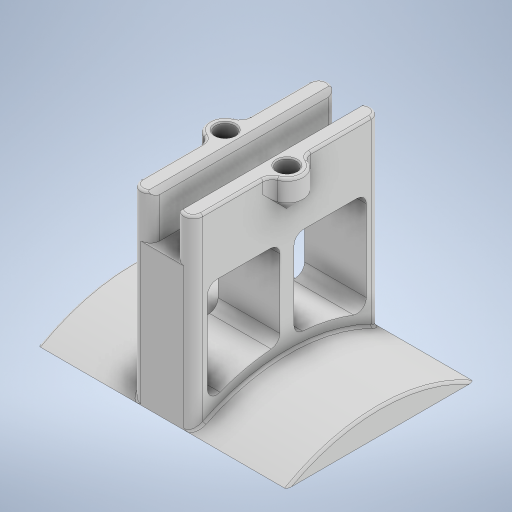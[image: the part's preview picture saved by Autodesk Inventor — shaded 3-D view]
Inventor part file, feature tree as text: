
AUTODESK INVENTOR PART (.ipt)
format: ipt  version: 2023 (Build 270158000, 158)  size: 468,992 bytes
history: native  units: mm
features: extrude x6, sketch x5, fillet x4, chamfer x3, plane x1, mirror x1
ambient origin geometry x8: Origin, YZ Plane, XZ Plane, XY Plane, X Axis, Y Axis, Z Axis, Center Point
bodies: Solid1 (feature_tree)
feature tree (20):
  extrude  "Extrusion1"  Depth=40.0mm
  extrude  "Extrusion2"  Depth=20.0mm TaperAngle=0.0deg
  plane  "Work Plane1"
  mirror  "Mirror1"
  extrude  "Extrusion3"  Depth=5.2mm
  sketch  "Sketch4"  dims[d9=4.0mm d10=9.6mm d11=0.0mm]
  extrude  "Extrusion4"  Depth=9.6mm TaperAngle=0.0deg
  extrude  "Extrusion5"  Depth=2.0mm TaperAngle=45.0deg
  extrude  "Extrusion6"  Depth=1.5mm
  chamfer  "Chamfer2"  Distance=7.0mm
  fillet  "Fillet1"  Radius=8.0mm
  chamfer  "Chamfer1"  Distance=3.1mm
  fillet  "Fillet2"  Radius=2.0mm
  fillet  "Fillet3"  Radius=2.0mm
  chamfer  "Chamfer3"  Distance=0.5mm
  fillet  "Fillet4"  Radius=2.0mm
  sketch  "Sketch1"  dims[d0=40.0mm d1=40.0mm]
  sketch  "Sketch2"  dims[d2=13.2mm d3=0.0mm d5=20.0mm d6=0.0mm]
  sketch  "Sketch3"  dims[d7=-6.6mm d8=5.2mm]
  sketch  "Sketch5"  dims[d12=2.0mm d13=1.0mm d14=2.0mm d15=45.0deg d16=4.1mm d17=7.0mm d18=8.0mm d19=0.0mm d20=3.1mm d21=0.0mm d22=3.5mm d23=2.0mm d24=45.0deg d25=2.0mm d26=0.5mm d27=0.25mm d28=2.0mm d29=45.0deg d30=40.0mm d31=3.0mm d32=3.0mm d33=4.0mm d34=4.0mm d35=40.0mm d36=3.1mm d37=0.0mm d38=2.0mm d39=3.0mm d40=1.5mm]
